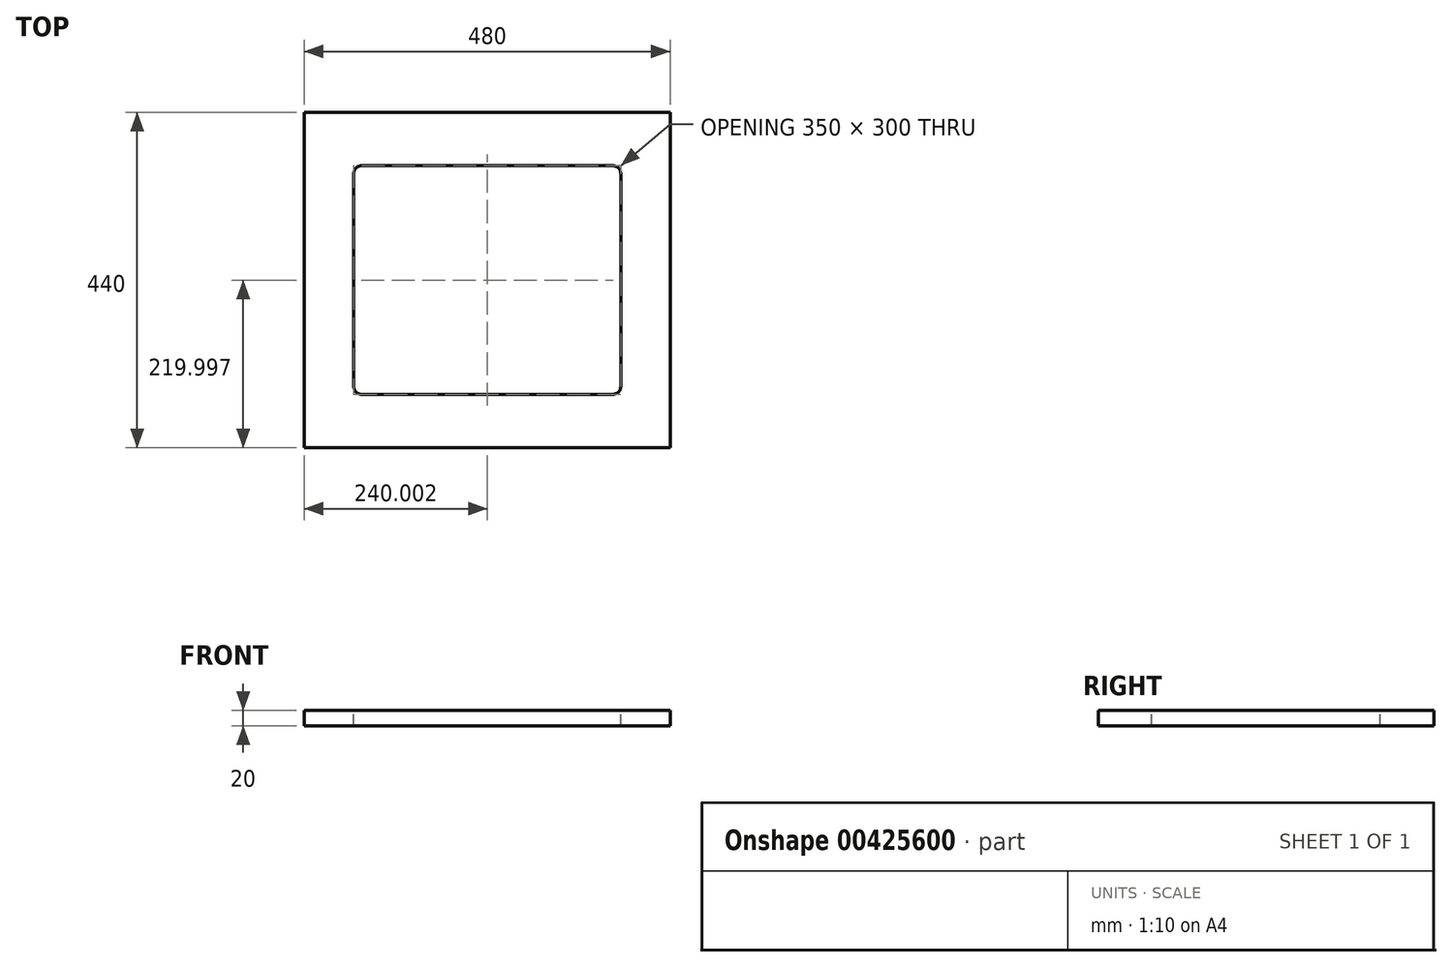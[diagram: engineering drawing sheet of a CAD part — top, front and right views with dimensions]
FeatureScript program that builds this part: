
annotation { "Feature Type Name" : "Feature", "Feature Type Description" : "" }
export const myFeature = defineFeature(function(context is Context, id is Id, definition is map)
    precondition{}
    {
        {
            var Q0;
            Q0=qCreatedBy(makeId("Top.planeOp"),FACE);
            var sketch = newSketch(context, id + "F0", { "sketchPlane" : qUnion([Q0])});
            skLineSegment(sketch, "E0.bottom", {"start": v(-244.63, 237.76) * mm, "end": v(235.37, 237.76) * mm});
            skLineSegment(sketch, "E0.top", {"start": v(-244.63, -202.24) * mm, "end": v(235.37, -202.24) * mm});
            skLineSegment(sketch, "E0.left", {"start": v(-244.63, 237.76) * mm, "end": v(-244.63, -202.24) * mm});
            skLineSegment(sketch, "E0.right", {"start": v(235.37, 237.76) * mm, "end": v(235.37, -202.24) * mm});
            skSolve(sketch);
        }
        {
            var Q0;
            Q0 = qSketchRegion(id + "F0", true);
            extrude(context, id + "F1", {"entities" : qUnion([Q0]), "depth" : 20 * mm});
        }
        {
            var Q0;
            Q0=makeQuery(id+"F1.opExtrude","CAP_FACE",FACE,{"disambiguationData":[OSD([sQuery(id+"F0.wireOp",EDGE,"E0.bottom"),sQuery(id+"F0.wireOp",EDGE,"E0.top"),sQuery(id+"F0.wireOp",EDGE,"E0.left"),sQuery(id+"F0.wireOp",EDGE,"E0.right")])],"isStart":false});
            var sketch = newSketch(context, id + "F2", { "sketchPlane" : qUnion([Q0])});
            skLineSegment(sketch, "E1.bottom", {"start": v(-179.63, 167.76) * mm, "end": v(-4.63, 167.76) * mm});
            skLineSegment(sketch, "E1.top", {"start": v(-179.63, 17.76) * mm, "end": v(-4.63, 17.76) * mm});
            skLineSegment(sketch, "E1.left", {"start": v(-179.63, 167.76) * mm, "end": v(-179.63, 17.76) * mm});
            skLineSegment(sketch, "E1.right", {"start": v(-4.63, 167.76) * mm, "end": v(-4.63, 17.76) * mm});
            skLineSegment(sketch, "E2", {"start": v(-4.63, 237.76) * mm, "end": v(-4.63, -202.24) * mm});
            skPoint(sketch, "E3.endSnap0", {"position": v(-244.63, 17.76) * mm});
            skLineSegment(sketch, "E4", {"start": v(-244.63, 17.76) * mm, "end": v(235.37, 17.76) * mm});
            skLineSegment(sketch, "E5.MirrorCS", {"start": v(-179.63, -132.24) * mm, "end": v(-4.63, -132.24) * mm});
            skLineSegment(sketch, "E6.MirrorCS", {"start": v(-179.63, -132.24) * mm, "end": v(-179.63, 17.76) * mm});
            skLineSegment(sketch, "E7.MirrorCS", {"start": v(-4.63, -132.24) * mm, "end": v(-4.63, 17.76) * mm});
            skLineSegment(sketch, "E8.MirrorCS", {"start": v(170.37, 17.76) * mm, "end": v(-4.63, 17.76) * mm});
            skLineSegment(sketch, "E9.MirrorCS", {"start": v(170.37, -132.24) * mm, "end": v(-4.63, -132.24) * mm});
            skLineSegment(sketch, "E10.MirrorCS", {"start": v(170.37, 167.76) * mm, "end": v(170.37, 17.76) * mm});
            skLineSegment(sketch, "E11.MirrorCS", {"start": v(170.37, -132.24) * mm, "end": v(170.37, 17.76) * mm});
            skLineSegment(sketch, "E12.MirrorCS", {"start": v(170.37, 167.76) * mm, "end": v(-4.63, 167.76) * mm});
            skSolve(sketch);
        }
        {
            var Q0;
            Q0 = qSketchRegion(id + "F2", true);
            extrude(context, id + "F3", {"entities" : qUnion([Q0]), "operationType" : NewBodyOperationType.REMOVE, "endBound" : BoundingType.UP_TO_NEXT, "oppositeDirection" : true, "depth" : 25 * mm});
        }
        {
            var Q0;
            Q0=makeQuery(id+"F3.boolean.opBoolean","COPY",EDGE,{"derivedFrom":makeQuery(id+"F3.opExtrude","SWEPT_EDGE",EDGE,{"disambiguationData":[OSD([sQuery(id+"F2.wireOp",EDGE,"E1.bottom"),sQuery(id+"F2.wireOp",EDGE,"E1.left")])]})});
            var Q1;
            Q1=makeQuery(id+"F3.boolean.opBoolean","COPY",EDGE,{"derivedFrom":makeQuery(id+"F3.opExtrude","SWEPT_EDGE",EDGE,{"disambiguationData":[OSD([sQuery(id+"F2.wireOp",EDGE,"E5.MirrorCS"),sQuery(id+"F2.wireOp",EDGE,"E6.MirrorCS")])]})});
            var Q2;
            Q2=makeQuery(id+"F3.boolean.opBoolean","COPY",EDGE,{"derivedFrom":makeQuery(id+"F3.opExtrude","SWEPT_EDGE",EDGE,{"disambiguationData":[OSD([sQuery(id+"F2.wireOp",EDGE,"E10.MirrorCS"),sQuery(id+"F2.wireOp",EDGE,"E12.MirrorCS")])]})});
            var Q3;
            Q3=makeQuery(id+"F3.boolean.opBoolean","COPY",EDGE,{"derivedFrom":makeQuery(id+"F3.opExtrude","SWEPT_EDGE",EDGE,{"disambiguationData":[OSD([sQuery(id+"F2.wireOp",EDGE,"E9.MirrorCS"),sQuery(id+"F2.wireOp",EDGE,"E11.MirrorCS")])]})});
            fillet(context, id + "F4", {"entities" : qUnion([Q0, Q1, Q2, Q3]), "radius" : 10 * mm, "tangentPropagation" : true, "allowEdgeOverflow" : false});
        }
    });
